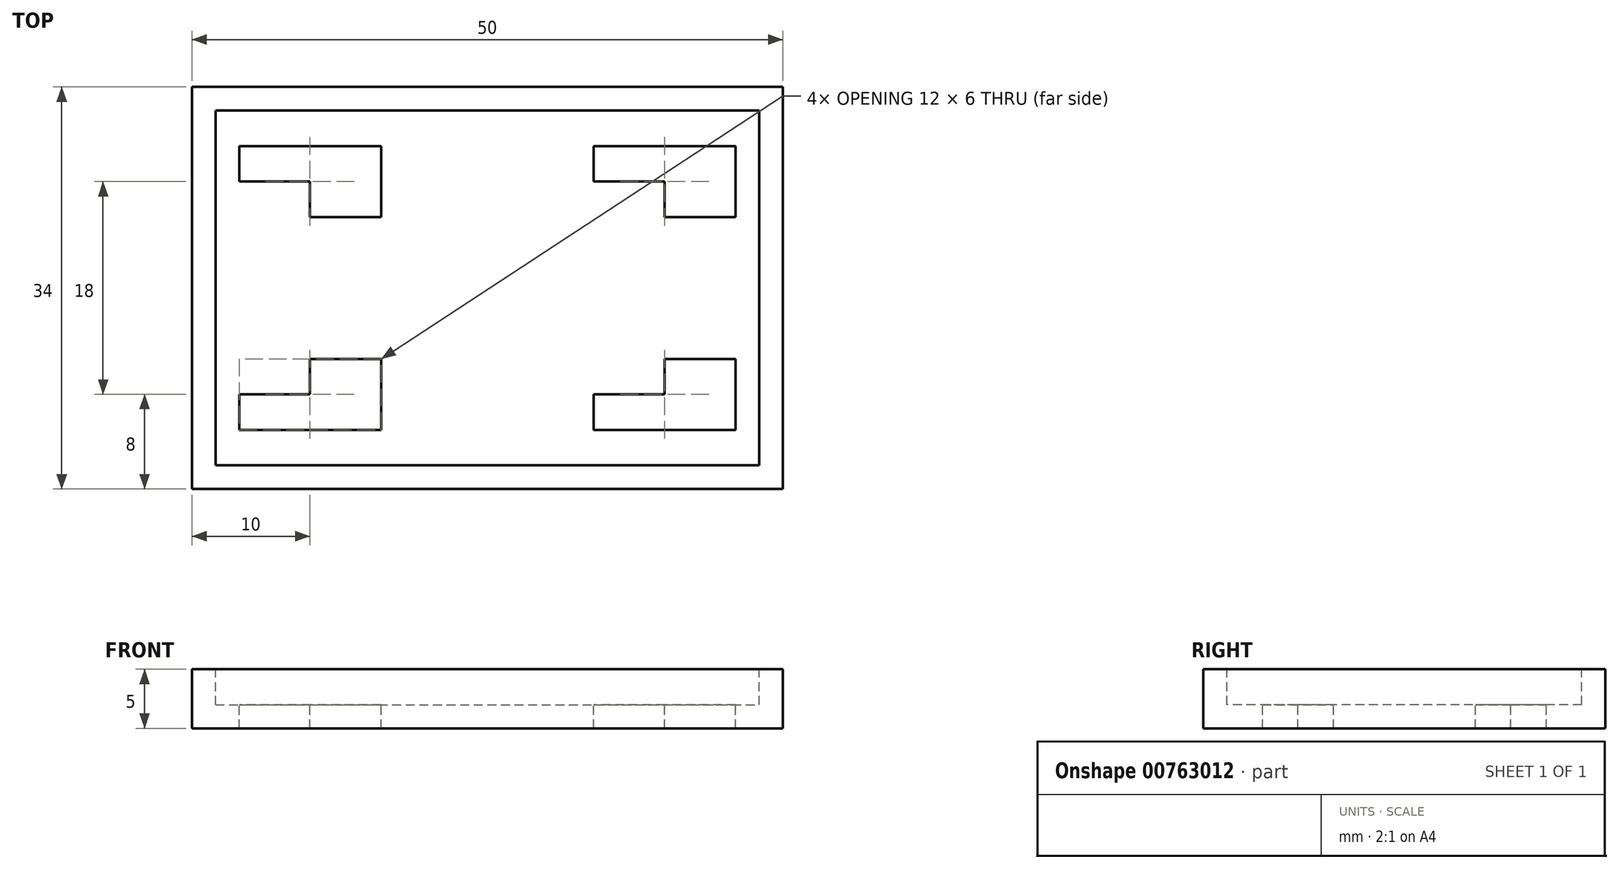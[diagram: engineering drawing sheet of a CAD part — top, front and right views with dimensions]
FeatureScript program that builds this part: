
annotation { "Feature Type Name" : "Feature", "Feature Type Description" : "" }
export const myFeature = defineFeature(function(context is Context, id is Id, definition is map)
    precondition{}
    {
        {
            var Q0;
            Q0=qCreatedBy(makeId("Top.planeOp"),FACE);
            var sketch = newSketch(context, id + "F0", { "sketchPlane" : qUnion([Q0])});
            skLineSegment(sketch, "E0.bottom", {"start": v(-25, 17) * mm, "end": v(25, 17) * mm});
            skLineSegment(sketch, "E0.top", {"start": v(-25, -17) * mm, "end": v(25, -17) * mm});
            skLineSegment(sketch, "E0.left", {"start": v(-25, 17) * mm, "end": v(-25, -17) * mm});
            skLineSegment(sketch, "E0.right", {"start": v(25, 17) * mm, "end": v(25, -17) * mm});
            skSolve(sketch);
        }
        {
            var Q0;
            Q0 = qSketchRegion(id + "F0", true);
            extrude(context, id + "F1", {"entities" : qUnion([Q0]), "depth" : 5 * mm, "offsetDistance" : 25 * mm});
        }
        {
            var Q0;
            Q0=makeQuery(id+"F1.opExtrude","CAP_FACE",FACE,{"disambiguationData":[OSD([sQuery(id+"F0.wireOp",EDGE,"E0.bottom"),sQuery(id+"F0.wireOp",EDGE,"E0.top"),sQuery(id+"F0.wireOp",EDGE,"E0.left"),sQuery(id+"F0.wireOp",EDGE,"E0.right")])],"isStart":false});
            var sketch = newSketch(context, id + "F2", { "sketchPlane" : qUnion([Q0])});
            skLineSegment(sketch, "E1.bottom", {"start": v(-23, 15) * mm, "end": v(23, 15) * mm});
            skLineSegment(sketch, "E1.top", {"start": v(-23, -15) * mm, "end": v(23, -15) * mm});
            skLineSegment(sketch, "E1.left", {"start": v(-23, 15) * mm, "end": v(-23, -15) * mm});
            skLineSegment(sketch, "E1.right", {"start": v(23, 15) * mm, "end": v(23, -15) * mm});
            skSolve(sketch);
        }
        {
            var Q0;
            Q0 = qSketchRegion(id + "F2", true);
            extrude(context, id + "F3", {"entities" : qUnion([Q0]), "operationType" : NewBodyOperationType.REMOVE, "oppositeDirection" : true, "depth" : 3 * mm, "offsetDistance" : 25 * mm});
        }
        {
            var Q0;
            Q0=makeQuery(id+"F3.boolean.opBoolean","COPY",FACE,{"derivedFrom":makeQuery(id+"F3.opExtrude","CAP_FACE",FACE,{"disambiguationData":[OSD([sQuery(id+"F2.wireOp",EDGE,"E1.bottom"),sQuery(id+"F2.wireOp",EDGE,"E1.top"),sQuery(id+"F2.wireOp",EDGE,"E1.left"),sQuery(id+"F2.wireOp",EDGE,"E1.right")])],"isStart":false})});
            var sketch = newSketch(context, id + "F4", { "sketchPlane" : qUnion([Q0])});
            skLineSegment(sketch, "E2", {"start": v(-21, 12) * mm, "end": v(-9, 12) * mm});
            skLineSegment(sketch, "E3", {"start": v(-9, 12) * mm, "end": v(-9, 6) * mm});
            skLineSegment(sketch, "E4", {"start": v(-9, 6) * mm, "end": v(-15, 6) * mm});
            skLineSegment(sketch, "E5", {"start": v(-15, 6) * mm, "end": v(-15, 9) * mm});
            skLineSegment(sketch, "E6", {"start": v(-15, 9) * mm, "end": v(-21, 9) * mm});
            skLineSegment(sketch, "E7", {"start": v(-21, 9) * mm, "end": v(-21, 12) * mm});
            skLineSegment(sketch, "E8", {"start": v(9, 12) * mm, "end": v(21, 12) * mm});
            skLineSegment(sketch, "E9", {"start": v(21, 12) * mm, "end": v(21, 6) * mm});
            skLineSegment(sketch, "E10", {"start": v(21, 6) * mm, "end": v(15, 6) * mm});
            skLineSegment(sketch, "E11", {"start": v(15, 6) * mm, "end": v(15, 9) * mm});
            skLineSegment(sketch, "E12", {"start": v(15, 9) * mm, "end": v(9, 9) * mm});
            skLineSegment(sketch, "E13", {"start": v(9, 9) * mm, "end": v(9, 12) * mm});
            skLineSegment(sketch, "E14.MirrorCS", {"start": v(-21, -9) * mm, "end": v(-21, -12) * mm});
            skLineSegment(sketch, "E15.MirrorCS", {"start": v(-21, -12) * mm, "end": v(-9, -12) * mm});
            skLineSegment(sketch, "E16.MirrorCS", {"start": v(-15, -9) * mm, "end": v(-21, -9) * mm});
            skLineSegment(sketch, "E17.MirrorCS", {"start": v(-15, -6) * mm, "end": v(-15, -9) * mm});
            skLineSegment(sketch, "E18.MirrorCS", {"start": v(-9, -6) * mm, "end": v(-15, -6) * mm});
            skLineSegment(sketch, "E19.MirrorCS", {"start": v(-9, -12) * mm, "end": v(-9, -6) * mm});
            skLineSegment(sketch, "E20.MirrorCS", {"start": v(9, -9) * mm, "end": v(9, -12) * mm});
            skLineSegment(sketch, "E21.MirrorCS", {"start": v(15, -9) * mm, "end": v(9, -9) * mm});
            skLineSegment(sketch, "E22.MirrorCS", {"start": v(15, -6) * mm, "end": v(15, -9) * mm});
            skLineSegment(sketch, "E23.MirrorCS", {"start": v(21, -6) * mm, "end": v(15, -6) * mm});
            skLineSegment(sketch, "E24.MirrorCS", {"start": v(21, -12) * mm, "end": v(21, -6) * mm});
            skLineSegment(sketch, "E25.MirrorCS", {"start": v(9, -12) * mm, "end": v(21, -12) * mm});
            skSolve(sketch);
        }
        {
            var Q0;
            Q0 = qSketchRegion(id + "F4", true);
            extrude(context, id + "F5", {"entities" : qUnion([Q0]), "operationType" : NewBodyOperationType.REMOVE, "oppositeDirection" : true, "depth" : 2 * mm, "offsetDistance" : 25 * mm});
        }
    });
